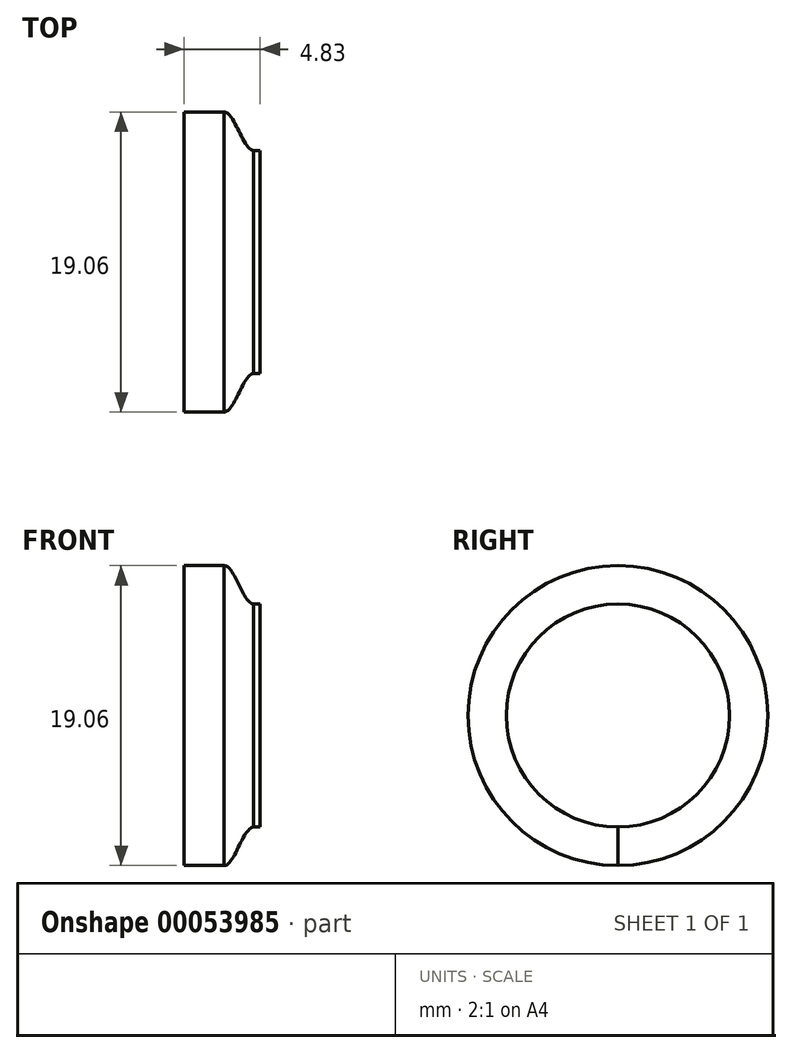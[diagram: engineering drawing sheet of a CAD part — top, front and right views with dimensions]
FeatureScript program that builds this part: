
annotation { "Feature Type Name" : "Feature", "Feature Type Description" : "" }
export const myFeature = defineFeature(function(context is Context, id is Id, definition is map)
    precondition{}
    {
        {
            var Q0;
            Q0=qCreatedBy(makeId("Right.planeOp"),FACE);
            var sketch = newSketch(context, id + "F0", { "sketchPlane" : qUnion([Q0])});
            skCircle(sketch, "E0", {"center": v(0, 0) * mm, "radius": 9.53 * mm});
            skSolve(sketch);
        }
        {
            var Q0;
            Q0 = qSketchRegion(id + "F0", true);
            extrude(context, id + "F1", {"entities" : qUnion([Q0]), "depth" : 2.54 * mm});
        }
        {
            var Q0;
            Q0=makeQuery(id+"F1.opExtrude","CAP_FACE",FACE,{"disambiguationData":[OSD([sQuery(id+"F0.wireOp",EDGE,"E0")])],"isStart":false});
            var sketch = newSketch(context, id + "F2", { "sketchPlane" : qUnion([Q0])});
            skCircle(sketch, "E1", {"center": v(0, 0) * mm, "radius": 7.08 * mm});
            skSolve(sketch);
        }
        {
            var Q0;
            Q0=makeQuery(id+"F2.imprint","IMPRINT",FACE,{"disambiguationData":[TD([[makeQuery(id+"F2.imprint","IMPRINT",EDGE,{"derivedFrom":sQuery(id+"F2.wireOp",EDGE,"E1")}),1.0]])]});
            extrude(context, id + "F3", {"entities" : qUnion([Q0]), "operationType" : NewBodyOperationType.ADD, "depth" : 2.3 * mm, "hasSecondDirection" : true, "secondDirectionOppositeDirection" : false, "secondDirectionDepth" : 1.87 * mm});
        }
        {
            var Q0;
            Q0=makeQuery(id+"F3.opExtrude","CAP_FACE",FACE,{"disambiguationData":[OSD([sQuery(id+"F2.wireOp",EDGE,"E1")])],"isStart":true});
            var Q1;
            Q1=makeQuery(id+"F1.opExtrude","CAP_FACE",FACE,{"disambiguationData":[OSD([sQuery(id+"F0.wireOp",EDGE,"E0")])],"isStart":false});
            loft(context, id + "F4", {"startCondition" : LoftEndDerivativeType.NORMAL_TO_PROFILE, "startMagnitude" : 1, "endCondition" : LoftEndDerivativeType.NORMAL_TO_PROFILE, "endMagnitude" : 1, "sheetProfilesArray" : [{ "sheetProfileEntities" : qUnion([Q0]) }, { "sheetProfileEntities" : qUnion([Q1]) }]});
        }
    });
